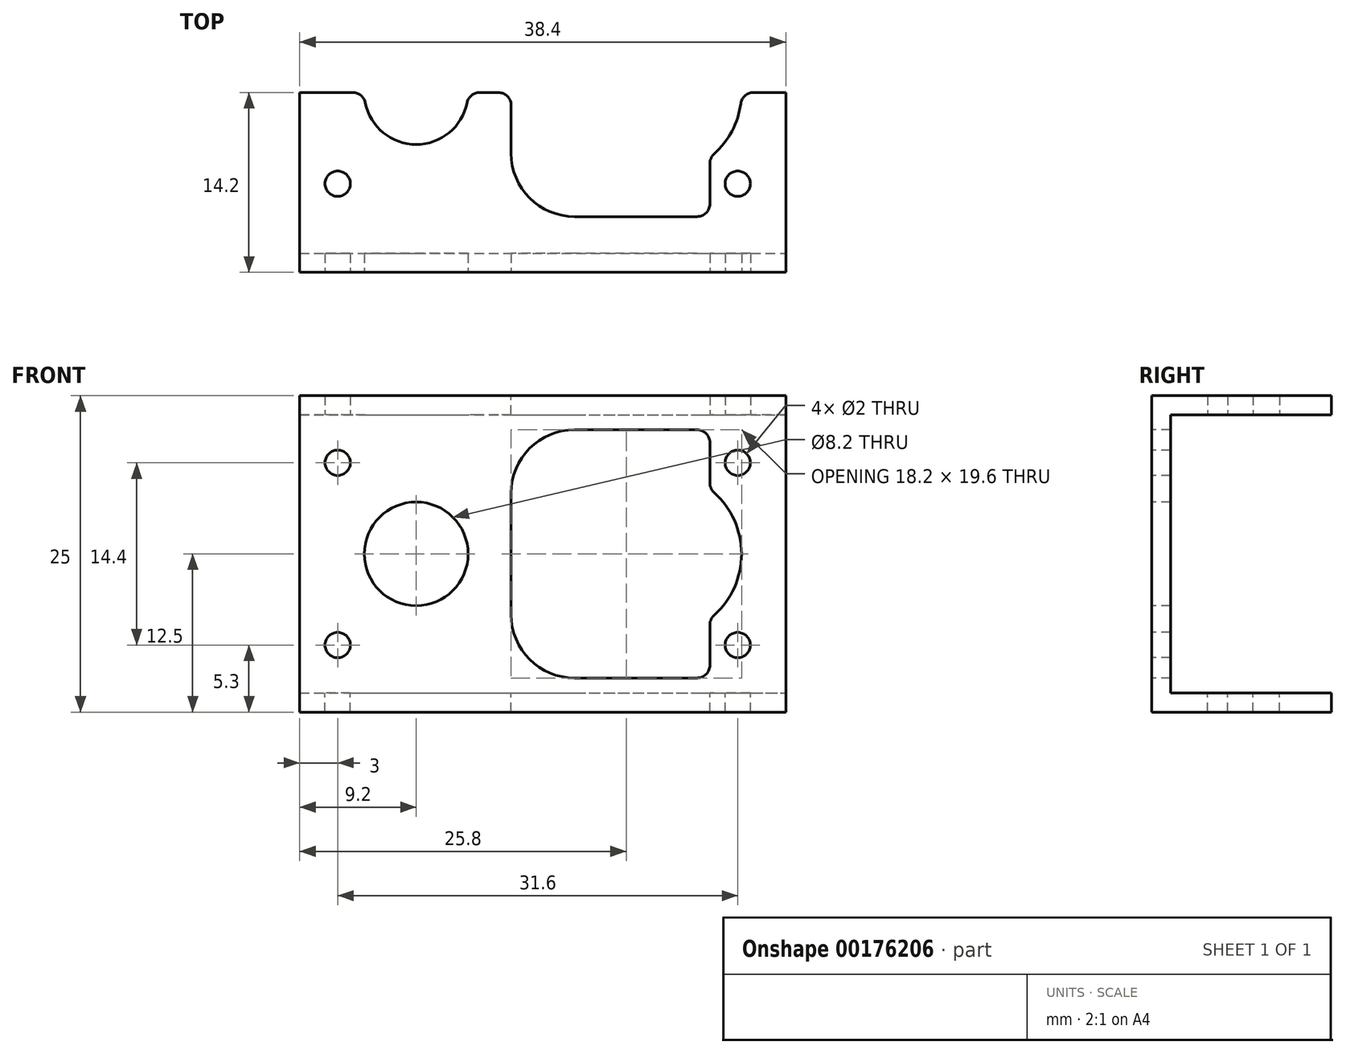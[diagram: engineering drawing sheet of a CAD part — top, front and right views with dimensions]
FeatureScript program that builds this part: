
annotation { "Feature Type Name" : "Feature", "Feature Type Description" : "" }
export const myFeature = defineFeature(function(context is Context, id is Id, definition is map)
    precondition{}
    {
        {
            var Q0;
            Q0=qCreatedBy(makeId("Top.planeOp"),FACE);
            var sketch = newSketch(context, id + "F0", { "sketchPlane" : qUnion([Q0])});
            skLineSegment(sketch, "E0.bottom", {"start": v(19.2, -14.2) * mm, "end": v(-19.2, -14.2) * mm});
            skLineSegment(sketch, "E0.top", {"start": v(19.2, 14.2) * mm, "end": v(-19.2, 14.2) * mm});
            skLineSegment(sketch, "E0.left", {"start": v(19.2, -14.2) * mm, "end": v(19.2, 14.2) * mm});
            skLineSegment(sketch, "E0.right", {"start": v(-19.2, -14.2) * mm, "end": v(-19.2, 14.2) * mm});
            skPoint(sketch, "E0.middle", {"position": v(0, 0) * mm});
            skCircle(sketch, "E1", {"center": v(-10, 0) * mm, "radius": 4.1 * mm});
            skCircle(sketch, "E2", {"center": v(-16.2, 7.2) * mm, "radius": 1 * mm});
            skCircle(sketch, "E3", {"center": v(15.4, 7.2) * mm, "radius": 1 * mm});
            skLineSegment(sketch, "E4.bottom", {"start": v(2.5, 9.8) * mm, "end": v(12.2, 9.8) * mm});
            skLineSegment(sketch, "E4.top", {"start": v(2.5, -9.8) * mm, "end": v(12.2, -9.8) * mm});
            skLineSegment(sketch, "E4.left", {"start": v(-2.5, 4.8) * mm, "end": v(-2.5, -4.8) * mm});
            skLineSegment(sketch, "E4.right", {"start": v(13.2, 8.8) * mm, "end": v(13.2, 5.6) * mm});
            skPoint(sketch, "E4.middle", {"position": v(5.35, 0) * mm});
            skPoint(sketch, "E5.visualSharp", {"position": v(-2.5, 9.8) * mm});
            skArc(sketch, "E5.filletArc", {"start": v(2.5, 9.8) * mm, "mid": v(-1.04, 8.34) * mm, "end": v(-2.5, 4.8) * mm});
            skPoint(sketch, "E6.visualSharp", {"position": v(-2.5, -9.8) * mm});
            skArc(sketch, "E6.filletArc", {"start": v(-2.5, -4.8) * mm, "mid": v(-1.04, -8.34) * mm, "end": v(2.5, -9.8) * mm});
            skPoint(sketch, "E7.visualSharp", {"position": v(13.2, 9.8) * mm});
            skArc(sketch, "E7.filletArc", {"start": v(13.2, 8.8) * mm, "mid": v(12.9, 9.5) * mm, "end": v(12.2, 9.8) * mm});
            skPoint(sketch, "E8.visualSharp", {"position": v(13.2, -9.8) * mm});
            skArc(sketch, "E8.filletArc", {"start": v(12.2, -9.8) * mm, "mid": v(12.9, -9.5) * mm, "end": v(13.2, -8.8) * mm});
            skCircle(sketch, "E9.MirrorC", {"center": v(-16.2, -7.2) * mm, "radius": 1 * mm});
            skCircle(sketch, "E10.MirrorC", {"center": v(15.4, -7.2) * mm, "radius": 1 * mm});
            skArc(sketch, "E11", {"start": v(13.53, -4.84) * mm, "mid": v(15.7, 0) * mm, "end": v(13.53, 4.84) * mm});
            skLineSegment(sketch, "E12.trimOffspring", {"start": v(13.2, -5.6) * mm, "end": v(13.2, -8.8) * mm});
            skPoint(sketch, "E13.visualSharp", {"position": v(13.2, 5.12) * mm});
            skArc(sketch, "E13.filletArc", {"start": v(13.2, 5.6) * mm, "mid": v(13.29, 5.18) * mm, "end": v(13.53, 4.84) * mm});
            skPoint(sketch, "E14.visualSharp", {"position": v(13.2, -5.12) * mm});
            skArc(sketch, "E14.filletArc", {"start": v(13.53, -4.84) * mm, "mid": v(13.29, -5.18) * mm, "end": v(13.2, -5.6) * mm});
            skSolve(sketch);
        }
        {
            var Q0;
            Q0=qSketchRegion(id+"F0",true);
            extrude(context, id + "F1", {"entities" : qUnion([Q0]), "depth" : 1.5 * mm});
        }
        {
            var Q0;
            Q0=makeQuery(id+"F1.opExtrude","CAP_FACE",FACE,{"disambiguationData":[OSD([sQuery(id+"F0.wireOp",EDGE,"E0.bottom"),sQuery(id+"F0.wireOp",EDGE,"E0.top"),sQuery(id+"F0.wireOp",EDGE,"E0.left"),sQuery(id+"F0.wireOp",EDGE,"E0.right"),sQuery(id+"F0.wireOp",EDGE,"E1"),sQuery(id+"F0.wireOp",EDGE,"E2"),sQuery(id+"F0.wireOp",EDGE,"E3"),sQuery(id+"F0.wireOp",EDGE,"E4.bottom"),sQuery(id+"F0.wireOp",EDGE,"E4.top"),sQuery(id+"F0.wireOp",EDGE,"E4.left"),sQuery(id+"F0.wireOp",EDGE,"E4.right"),sQuery(id+"F0.wireOp",EDGE,"E5.filletArc"),sQuery(id+"F0.wireOp",EDGE,"E6.filletArc"),sQuery(id+"F0.wireOp",EDGE,"E7.filletArc"),sQuery(id+"F0.wireOp",EDGE,"E8.filletArc"),sQuery(id+"F0.wireOp",EDGE,"E9.MirrorC"),sQuery(id+"F0.wireOp",EDGE,"E10.MirrorC"),sQuery(id+"F0.wireOp",EDGE,"E11"),sQuery(id+"F0.wireOp",EDGE,"E12.trimOffspring"),sQuery(id+"F0.wireOp",EDGE,"E13.filletArc"),sQuery(id+"F0.wireOp",EDGE,"E14.filletArc")])],"isStart":true});
            var sketch = newSketch(context, id + "F2", { "sketchPlane" : qUnion([Q0])});
            skLineSegment(sketch, "E15.bottom", {"start": v(-19.2, 14.2) * mm, "end": v(19.2, 14.2) * mm});
            skLineSegment(sketch, "E15.top", {"start": v(-19.2, 12.7) * mm, "end": v(19.2, 12.7) * mm});
            skLineSegment(sketch, "E15.left", {"start": v(-19.2, 14.2) * mm, "end": v(-19.2, 12.7) * mm});
            skLineSegment(sketch, "E15.right", {"start": v(19.2, 14.2) * mm, "end": v(19.2, 12.7) * mm});
            skSolve(sketch);
        }
        {
            var Q0;
            Q0=qSketchRegion(id+"F2",true);
            extrude(context, id + "F3", {"entities" : qUnion([Q0]), "operationType" : NewBodyOperationType.ADD, "depth" : (29.3 - 3.8 - 3.5) * mm});
        }
        {
            var Q0;
            Q0=qCreatedBy(makeId("Top.planeOp"),FACE);
            cPlane(context, id + "F4", {"entities" : qUnion([Q0]), "cplaneType" : CPlaneType.OFFSET, "offset" : 11 * mm, "oppositeDirection" : true, "width" : 150 * mm, "height" : 150 * mm});
        }
        {
            var Q0;
            Q0=makeQuery(id+"F1.opExtrude","SWEPT_BODY",BODY,{"disambiguationData":[OSD([sQuery(id+"F0.wireOp",EDGE,"E0.bottom"),sQuery(id+"F0.wireOp",EDGE,"E0.top"),sQuery(id+"F0.wireOp",EDGE,"E0.left"),sQuery(id+"F0.wireOp",EDGE,"E0.right"),sQuery(id+"F0.wireOp",EDGE,"E1"),sQuery(id+"F0.wireOp",EDGE,"E2"),sQuery(id+"F0.wireOp",EDGE,"E3"),sQuery(id+"F0.wireOp",EDGE,"E4.bottom"),sQuery(id+"F0.wireOp",EDGE,"E4.top"),sQuery(id+"F0.wireOp",EDGE,"E4.left"),sQuery(id+"F0.wireOp",EDGE,"E4.right"),sQuery(id+"F0.wireOp",EDGE,"E5.filletArc"),sQuery(id+"F0.wireOp",EDGE,"E6.filletArc"),sQuery(id+"F0.wireOp",EDGE,"E7.filletArc"),sQuery(id+"F0.wireOp",EDGE,"E8.filletArc"),sQuery(id+"F0.wireOp",EDGE,"E9.MirrorC"),sQuery(id+"F0.wireOp",EDGE,"E10.MirrorC"),sQuery(id+"F0.wireOp",EDGE,"E11"),sQuery(id+"F0.wireOp",EDGE,"E12.trimOffspring"),sQuery(id+"F0.wireOp",EDGE,"E13.filletArc"),sQuery(id+"F0.wireOp",EDGE,"E14.filletArc")])]});
            var Q1;
            Q1=qCreatedBy(id+"F4.planeOp",FACE);
            mirror(context, id + "F5", {"operationType" : NewBodyOperationType.ADD, "entities" : qUnion([Q0]), "mirrorPlane" : qUnion([Q1])});
        }
        {
            var Q0;
            Q0=makeQuery(id+"F5.opPattern","COPY",FACE,{"derivedFrom":makeQuery(id+"F1.opExtrude","CAP_FACE",FACE,{"disambiguationData":[OSD([sQuery(id+"F0.wireOp",EDGE,"E0.bottom"),sQuery(id+"F0.wireOp",EDGE,"E0.top"),sQuery(id+"F0.wireOp",EDGE,"E0.left"),sQuery(id+"F0.wireOp",EDGE,"E0.right"),sQuery(id+"F0.wireOp",EDGE,"E1"),sQuery(id+"F0.wireOp",EDGE,"E2"),sQuery(id+"F0.wireOp",EDGE,"E3"),sQuery(id+"F0.wireOp",EDGE,"E4.bottom"),sQuery(id+"F0.wireOp",EDGE,"E4.top"),sQuery(id+"F0.wireOp",EDGE,"E4.left"),sQuery(id+"F0.wireOp",EDGE,"E4.right"),sQuery(id+"F0.wireOp",EDGE,"E5.filletArc"),sQuery(id+"F0.wireOp",EDGE,"E6.filletArc"),sQuery(id+"F0.wireOp",EDGE,"E7.filletArc"),sQuery(id+"F0.wireOp",EDGE,"E8.filletArc"),sQuery(id+"F0.wireOp",EDGE,"E9.MirrorC"),sQuery(id+"F0.wireOp",EDGE,"E10.MirrorC"),sQuery(id+"F0.wireOp",EDGE,"E11"),sQuery(id+"F0.wireOp",EDGE,"E12.trimOffspring"),sQuery(id+"F0.wireOp",EDGE,"E13.filletArc"),sQuery(id+"F0.wireOp",EDGE,"E14.filletArc")])],"isStart":false}),"instanceName":"1"});
            var sketch = newSketch(context, id + "F6", { "sketchPlane" : qUnion([Q0])});
            skLineSegment(sketch, "E16.bottom", {"start": v(-19.2, -14.2) * mm, "end": v(19.2, -14.2) * mm});
            skLineSegment(sketch, "E16.top", {"start": v(-19.2, 0) * mm, "end": v(19.2, 0) * mm});
            skLineSegment(sketch, "E16.left", {"start": v(-19.2, -14.2) * mm, "end": v(-19.2, 0) * mm});
            skLineSegment(sketch, "E16.right", {"start": v(19.2, -14.2) * mm, "end": v(19.2, 0) * mm});
            skSolve(sketch);
        }
        {
            var Q0;
            Q0=qSketchRegion(id+"F6",true);
            extrude(context, id + "F7", {"entities" : qUnion([Q0]), "operationType" : NewBodyOperationType.REMOVE, "endBound" : BoundingType.THROUGH_ALL, "oppositeDirection" : true, "depth" : 25 * mm});
        }
        {
            var Q0;
            {var subQ0=makeQuery(id+"F3.boolean.opBoolean","MERGE",FACE,{"derivedFrom":[makeQuery(id+"F1.opExtrude","SWEPT_FACE",FACE,{"disambiguationData":[OSD([sQuery(id+"F0.wireOp",EDGE,"E0.bottom")])]}),makeQuery(id+"F3.opExtrude","SWEPT_FACE",FACE,{"disambiguationData":[OSD([sQuery(id+"F2.wireOp",EDGE,"E15.bottom")])]})]});Q0=makeQuery(id+"F5.boolean.opBoolean","MERGE",FACE,{"derivedFrom":[subQ0,makeQuery(id+"F5.opPattern","COPY",FACE,{"derivedFrom":subQ0,"instanceName":"1"})]});}
            var sketch = newSketch(context, id + "F8", { "sketchPlane" : qUnion([Q0])});
            skLineSegment(sketch, "E17", {"start": v(-19.2, -11) * mm, "end": v(19.2, -11) * mm, "construction": true});
            skCircle(sketch, "E18", {"center": v(-10, -11) * mm, "radius": 4.1 * mm});
            skCircle(sketch, "E19", {"center": v(-16.2, -3.8) * mm, "radius": 1 * mm});
            skCircle(sketch, "E20", {"center": v(15.4, -3.8) * mm, "radius": 1 * mm});
            skLineSegment(sketch, "E21.bottom", {"start": v(2.5, -1.2) * mm, "end": v(12.2, -1.2) * mm});
            skLineSegment(sketch, "E21.top", {"start": v(2.5, -20.8) * mm, "end": v(12.2, -20.8) * mm});
            skLineSegment(sketch, "E21.left", {"start": v(-2.5, -6.2) * mm, "end": v(-2.5, -15.8) * mm});
            skLineSegment(sketch, "E21.right", {"start": v(13.2, -2.2) * mm, "end": v(13.2, -5.4) * mm});
            skPoint(sketch, "E21.middle", {"position": v(5.35, -11) * mm});
            skPoint(sketch, "E22.visualSharp", {"position": v(-2.5, -1.2) * mm});
            skArc(sketch, "E22.filletArc", {"start": v(2.5, -1.2) * mm, "mid": v(-1.04, -2.66) * mm, "end": v(-2.5, -6.2) * mm});
            skPoint(sketch, "E23.visualSharp", {"position": v(-2.5, -20.8) * mm});
            skArc(sketch, "E23.filletArc", {"start": v(-2.5, -15.8) * mm, "mid": v(-1.04, -19.34) * mm, "end": v(2.5, -20.8) * mm});
            skPoint(sketch, "E24.visualSharp", {"position": v(13.2, -1.2) * mm});
            skArc(sketch, "E24.filletArc", {"start": v(13.2, -2.2) * mm, "mid": v(12.9, -1.5) * mm, "end": v(12.2, -1.2) * mm});
            skPoint(sketch, "E25.visualSharp", {"position": v(13.2, -20.8) * mm});
            skArc(sketch, "E25.filletArc", {"start": v(12.2, -20.8) * mm, "mid": v(12.9, -20.5) * mm, "end": v(13.2, -19.8) * mm});
            skArc(sketch, "E26", {"start": v(13.53, -15.84) * mm, "mid": v(15.7, -11) * mm, "end": v(13.53, -6.16) * mm});
            skLineSegment(sketch, "E27.trimOffspring", {"start": v(13.2, -16.6) * mm, "end": v(13.2, -19.8) * mm});
            skPoint(sketch, "E28.visualSharp", {"position": v(13.2, -5.88) * mm});
            skArc(sketch, "E28.filletArc", {"start": v(13.2, -5.4) * mm, "mid": v(13.29, -5.82) * mm, "end": v(13.53, -6.16) * mm});
            skPoint(sketch, "E29.visualSharp", {"position": v(13.2, -16.12) * mm});
            skArc(sketch, "E29.filletArc", {"start": v(13.53, -15.84) * mm, "mid": v(13.29, -16.18) * mm, "end": v(13.2, -16.6) * mm});
            skCircle(sketch, "E30.MirrorC", {"center": v(-16.2, -18.2) * mm, "radius": 1 * mm});
            skCircle(sketch, "E31.MirrorC", {"center": v(15.4, -18.2) * mm, "radius": 1 * mm});
            skSolve(sketch);
        }
        {
            var Q0;
            Q0=qSketchRegion(id+"F8",true);
            extrude(context, id + "F9", {"entities" : qUnion([Q0]), "operationType" : NewBodyOperationType.REMOVE, "endBound" : BoundingType.UP_TO_NEXT, "oppositeDirection" : true, "depth" : 25 * mm});
        }
        {
            var Q0;
            Q0=makeQuery(id+"F7.boolean.opBoolean","COPY",EDGE,{"disambiguationData":[OD(0.0)],"derivedFrom":makeQuery(id+"F7.opExtrude","SWEPT_EDGE",EDGE,{"disambiguationData":[OSD([sQuery(id+"F0.wireOp",EDGE,"E0.right"),sQuery(id+"F6.wireOp",EDGE,"E16.top"),sQuery(id+"F6.wireOp",EDGE,"E16.left")])]})});
            var Q1;
            Q1=makeQuery(id+"F7.boolean.opBoolean","COPY",EDGE,{"disambiguationData":[OD(1.0)],"derivedFrom":makeQuery(id+"F7.opExtrude","SWEPT_EDGE",EDGE,{"disambiguationData":[OSD([sQuery(id+"F0.wireOp",EDGE,"E0.right"),sQuery(id+"F6.wireOp",EDGE,"E16.top"),sQuery(id+"F6.wireOp",EDGE,"E16.left")])]})});
            var Q2;
            Q2=makeQuery(id+"F7.boolean.opBoolean","INTERSECT",EDGE,{"disambiguationData":[OD(1.0)],"derivedFrom":[makeQuery(id+"F1.opExtrude","SWEPT_FACE",FACE,{"disambiguationData":[OSD([sQuery(id+"F0.wireOp",EDGE,"E1")])]}),makeQuery(id+"F7.opExtrude","SWEPT_FACE",FACE,{"disambiguationData":[OSD([sQuery(id+"F6.wireOp",EDGE,"E16.top")])]})]});
            var Q3;
            Q3=makeQuery(id+"F7.boolean.opBoolean","INTERSECT",EDGE,{"disambiguationData":[OD(1.0)],"derivedFrom":[makeQuery(id+"F5.opPattern","COPY",FACE,{"derivedFrom":makeQuery(id+"F1.opExtrude","SWEPT_FACE",FACE,{"disambiguationData":[OSD([sQuery(id+"F0.wireOp",EDGE,"E1")])]}),"instanceName":"1"}),makeQuery(id+"F7.opExtrude","SWEPT_FACE",FACE,{"disambiguationData":[OSD([sQuery(id+"F6.wireOp",EDGE,"E16.top")])]})]});
            var Q4;
            Q4=makeQuery(id+"F7.boolean.opBoolean","INTERSECT",EDGE,{"disambiguationData":[OD(0.0)],"derivedFrom":[makeQuery(id+"F5.opPattern","COPY",FACE,{"derivedFrom":makeQuery(id+"F1.opExtrude","SWEPT_FACE",FACE,{"disambiguationData":[OSD([sQuery(id+"F0.wireOp",EDGE,"E1")])]}),"instanceName":"1"}),makeQuery(id+"F7.opExtrude","SWEPT_FACE",FACE,{"disambiguationData":[OSD([sQuery(id+"F6.wireOp",EDGE,"E16.top")])]})]});
            var Q5;
            Q5=makeQuery(id+"F7.boolean.opBoolean","INTERSECT",EDGE,{"derivedFrom":[makeQuery(id+"F5.opPattern","COPY",FACE,{"derivedFrom":makeQuery(id+"F1.opExtrude","SWEPT_FACE",FACE,{"disambiguationData":[OSD([sQuery(id+"F0.wireOp",EDGE,"E4.left")])]}),"instanceName":"1"}),makeQuery(id+"F7.opExtrude","SWEPT_FACE",FACE,{"disambiguationData":[OSD([sQuery(id+"F6.wireOp",EDGE,"E16.top")])]})]});
            var Q6;
            Q6=makeQuery(id+"F7.boolean.opBoolean","INTERSECT",EDGE,{"disambiguationData":[OD(0.0)],"derivedFrom":[makeQuery(id+"F1.opExtrude","SWEPT_FACE",FACE,{"disambiguationData":[OSD([sQuery(id+"F0.wireOp",EDGE,"E1")])]}),makeQuery(id+"F7.opExtrude","SWEPT_FACE",FACE,{"disambiguationData":[OSD([sQuery(id+"F6.wireOp",EDGE,"E16.top")])]})]});
            var Q7;
            Q7=makeQuery(id+"F7.boolean.opBoolean","INTERSECT",EDGE,{"derivedFrom":[makeQuery(id+"F5.opPattern","COPY",FACE,{"derivedFrom":makeQuery(id+"F1.opExtrude","SWEPT_FACE",FACE,{"disambiguationData":[OSD([sQuery(id+"F0.wireOp",EDGE,"E11")])]}),"instanceName":"1"}),makeQuery(id+"F7.opExtrude","SWEPT_FACE",FACE,{"disambiguationData":[OSD([sQuery(id+"F6.wireOp",EDGE,"E16.top")])]})]});
            var Q8;
            Q8=makeQuery(id+"F7.boolean.opBoolean","INTERSECT",EDGE,{"derivedFrom":[makeQuery(id+"F1.opExtrude","SWEPT_FACE",FACE,{"disambiguationData":[OSD([sQuery(id+"F0.wireOp",EDGE,"E11")])]}),makeQuery(id+"F7.opExtrude","SWEPT_FACE",FACE,{"disambiguationData":[OSD([sQuery(id+"F6.wireOp",EDGE,"E16.top")])]})]});
            var Q9;
            Q9=makeQuery(id+"F7.boolean.opBoolean","COPY",EDGE,{"disambiguationData":[OD(0.0)],"derivedFrom":makeQuery(id+"F7.opExtrude","SWEPT_EDGE",EDGE,{"disambiguationData":[OSD([sQuery(id+"F0.wireOp",EDGE,"E0.left"),sQuery(id+"F6.wireOp",EDGE,"E16.top"),sQuery(id+"F6.wireOp",EDGE,"E16.right")])]})});
            var Q10;
            Q10=makeQuery(id+"F7.boolean.opBoolean","INTERSECT",EDGE,{"derivedFrom":[makeQuery(id+"F1.opExtrude","SWEPT_FACE",FACE,{"disambiguationData":[OSD([sQuery(id+"F0.wireOp",EDGE,"E4.left")])]}),makeQuery(id+"F7.opExtrude","SWEPT_FACE",FACE,{"disambiguationData":[OSD([sQuery(id+"F6.wireOp",EDGE,"E16.top")])]})]});
            var Q11;
            Q11=makeQuery(id+"F7.boolean.opBoolean","COPY",EDGE,{"disambiguationData":[OD(1.0)],"derivedFrom":makeQuery(id+"F7.opExtrude","SWEPT_EDGE",EDGE,{"disambiguationData":[OSD([sQuery(id+"F0.wireOp",EDGE,"E0.left"),sQuery(id+"F6.wireOp",EDGE,"E16.top"),sQuery(id+"F6.wireOp",EDGE,"E16.right")])]})});
            fillet(context, id + "F10", {"entities" : qUnion([Q0, Q1, Q2, Q3, Q4, Q5, Q6, Q7, Q8, Q9, Q10, Q11]), "radius" : 1 * mm, "tangentPropagation" : true, "allowEdgeOverflow" : false});
        }
    });
